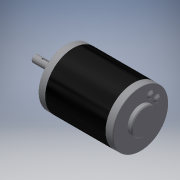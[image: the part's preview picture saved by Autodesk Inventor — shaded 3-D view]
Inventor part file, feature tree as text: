
AUTODESK INVENTOR PART (.ipt)
format: ipt  version: 2019 (Build 230136000, 136)  size: 162,816 bytes
history: native  units: in
note: dims shown in document units (in); Inventor stores cm internally (conversion verified against a paired STEP export)
features: chamfer x1
ambient origin geometry x8: Origin, YZ Plane, XZ Plane, XY Plane, X Axis, Y Axis, Z Axis, Center Point
bodies: Solid1 (feature_tree)
feature tree (1):
  chamfer  "Chamfer3"  [1 undecoded]
note: 1 required parameter value undecoded (feature->parameter linkage not recoverable at this tier; creation-order binding heuristic only, values carry confidence <= 0.55)
